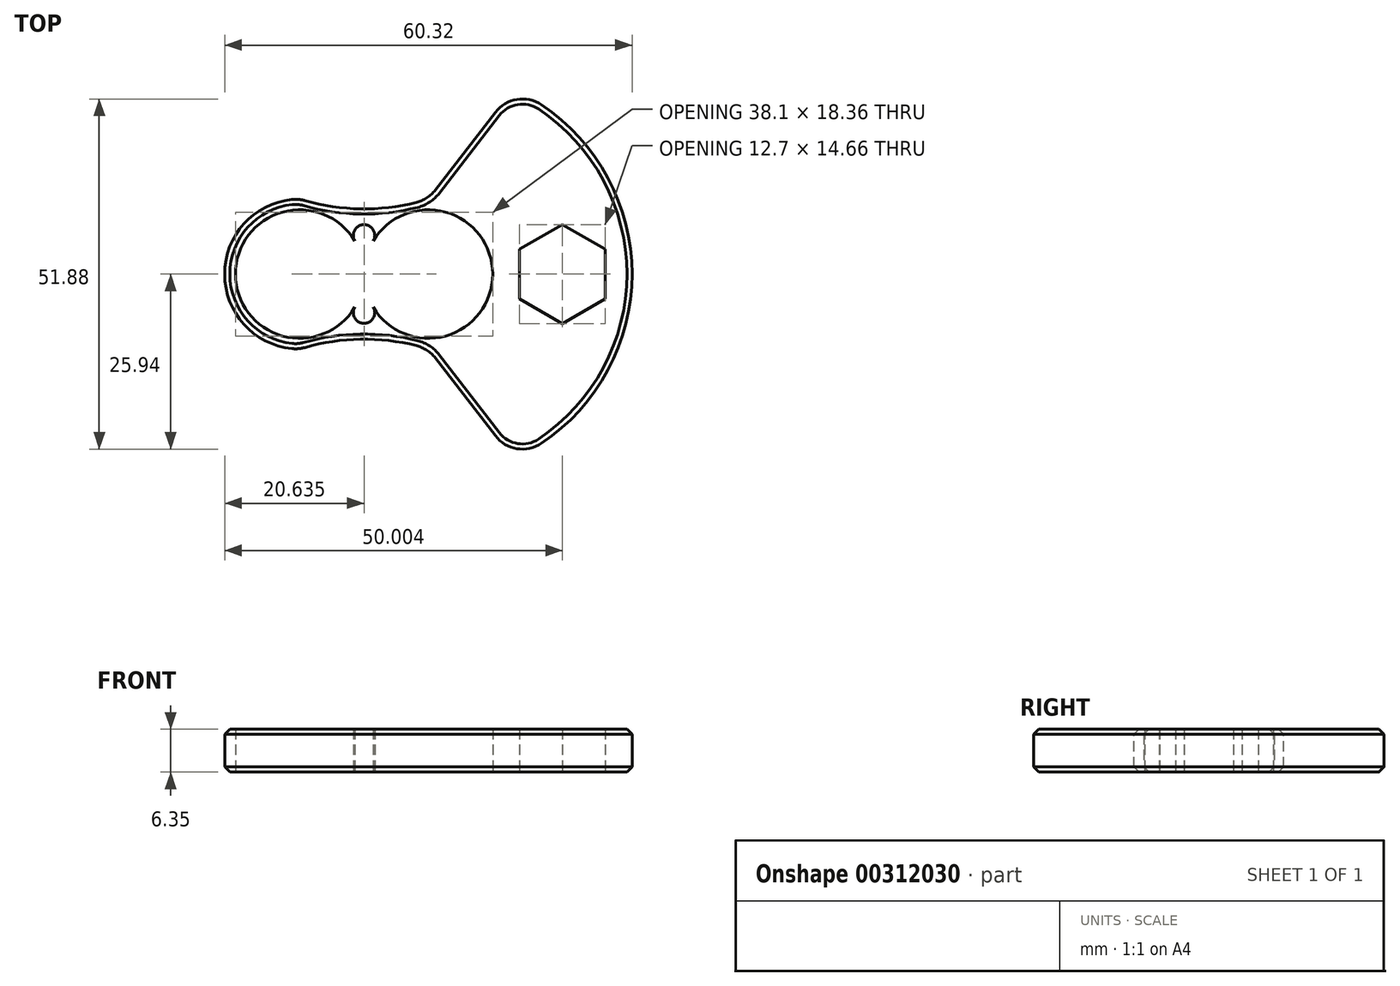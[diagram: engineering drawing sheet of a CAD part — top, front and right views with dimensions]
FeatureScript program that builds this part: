
annotation { "Feature Type Name" : "Feature", "Feature Type Description" : "" }
export const myFeature = defineFeature(function(context is Context, id is Id, definition is map)
    precondition{}
    {
        {
            var Q0;
            Q0=qCreatedBy(makeId("Top.planeOp"),FACE);
            var sketch = newSketch(context, id + "F0", { "sketchPlane" : qUnion([Q0])});
            skArc(sketch, "E0", {"start": v(-8.16, -4.9) * mm, "mid": v(9.52, 0) * mm, "end": v(-8.16, 4.9) * mm});
            skArc(sketch, "E1", {"start": v(-10.89, 4.9) * mm, "mid": v(-28.58, 0) * mm, "end": v(-10.89, -4.9) * mm});
            skArc(sketch, "E2", {"start": v(-19.05, 11.11) * mm, "mid": v(-30.16, 0) * mm, "end": v(-19.05, -11.11) * mm});
            skLineSegment(sketch, "E3", {"start": v(0, -11.11) * mm, "end": v(12.58, -27.42) * mm});
            skLineSegment(sketch, "E4", {"start": v(0, 11.11) * mm, "end": v(12.58, 27.42) * mm});
            skArc(sketch, "E5", {"start": v(-10.89, -4.9) * mm, "mid": v(-9.52, -7.31) * mm, "end": v(-8.16, -4.9) * mm});
            skArc(sketch, "E6", {"start": v(-8.16, 4.9) * mm, "mid": v(-9.53, 7.31) * mm, "end": v(-10.89, 4.9) * mm});
            skArc(sketch, "E7", {"start": v(12.58, -27.42) * mm, "mid": v(30.16, 0) * mm, "end": v(12.58, 27.42) * mm});
            skArc(sketch, "E8", {"start": v(-19.05, 11.11) * mm, "mid": v(-9.53, 9.65) * mm, "end": v(0, 11.11) * mm});
            skArc(sketch, "E9", {"start": v(0, -11.11) * mm, "mid": v(-9.53, -9.65) * mm, "end": v(-19.05, -11.11) * mm});
            skLineSegment(sketch, "E10.0", {"start": v(13.5, -3.67) * mm, "end": v(13.5, 3.67) * mm});
            skLineSegment(sketch, "E10.1", {"start": v(13.5, 3.67) * mm, "end": v(19.84, 7.33) * mm});
            skLineSegment(sketch, "E10.2", {"start": v(19.84, 7.33) * mm, "end": v(26.2, 3.67) * mm});
            skLineSegment(sketch, "E10.3", {"start": v(26.2, 3.67) * mm, "end": v(26.2, -3.67) * mm});
            skLineSegment(sketch, "E10.4", {"start": v(26.2, -3.67) * mm, "end": v(19.84, -7.33) * mm});
            skLineSegment(sketch, "E10.5", {"start": v(19.84, -7.33) * mm, "end": v(13.5, -3.67) * mm});
            skPoint(sketch, "E10.0.midPoint", {"position": v(13.5, 0) * mm});
            skPoint(sketch, "E11.center.orphan", {"position": v(19.84, 0) * mm});
            skPoint(sketch, "E12.start.orphan", {"position": v(9.52, 0) * mm});
            skPoint(sketch, "E13.trimOffspring.end.orphan", {"position": v(30.16, 0) * mm});
            skSolve(sketch);
        }
        {
            var Q0;
            Q0=makeQuery(id+"F0.imprint","IMPRINT",FACE,{"disambiguationData":[TD([[makeQuery(id+"F0.imprint","IMPRINT",EDGE,{"derivedFrom":sQuery(id+"F0.wireOp",EDGE,"E0")}),-1.0]])]});
            extrude(context, id + "F1", {"entities" : qUnion([Q0]), "depth" : 6.35 * mm, "offsetDistance" : 25.4 * mm});
        }
        {
            var Q0;
            Q0=makeQuery(id+"F1.opExtrude","SWEPT_EDGE",EDGE,{"disambiguationData":[OSD([sQuery(id+"F0.wireOp",EDGE,"kZLvEBYJ-JnEX-xgXO-vPxD-7ih4jmy4RvpC"),sQuery(id+"F0.wireOp",EDGE,"E3")])]});
            var Q1;
            Q1=makeQuery(id+"F1.opExtrude","SWEPT_EDGE",EDGE,{"disambiguationData":[OSD([sQuery(id+"F0.wireOp",EDGE,"kZLvEBYJ-JnEX-xgXO-vPxD-7ih4jmy4RvpC"),sQuery(id+"F0.wireOp",EDGE,"E4")])]});
            var Q2;
            Q2=makeQuery(id+"F1.opExtrude","SWEPT_EDGE",EDGE,{"disambiguationData":[OSD([sQuery(id+"F0.wireOp",EDGE,"E2"),sQuery(id+"F0.wireOp",EDGE,"AoVct10g-OvvF-BB1q-fatW-92vV8a4QILmj")])]});
            var Q3;
            Q3=makeQuery(id+"F1.opExtrude","SWEPT_EDGE",EDGE,{"disambiguationData":[OSD([sQuery(id+"F0.wireOp",EDGE,"E2"),sQuery(id+"F0.wireOp",EDGE,"D37h3eVz-aBzz-mAJ8-7cKl-PauLEiSiHLsy")])]});
            var Q4;
            Q4=makeQuery(id+"F1.opExtrude","SWEPT_EDGE",EDGE,{"disambiguationData":[OSD([sQuery(id+"F0.wireOp",EDGE,"E3"),sQuery(id+"F0.wireOp",EDGE,"AoVct10g-OvvF-BB1q-fatW-92vV8a4QILmj")])]});
            var Q5;
            Q5=makeQuery(id+"F1.opExtrude","SWEPT_EDGE",EDGE,{"disambiguationData":[OSD([sQuery(id+"F0.wireOp",EDGE,"E4"),sQuery(id+"F0.wireOp",EDGE,"D37h3eVz-aBzz-mAJ8-7cKl-PauLEiSiHLsy")])]});
            fillet(context, id + "F2", {"entities" : qUnion([Q0, Q1, Q2, Q3, Q4, Q5]), "radius" : 5.08 * mm, "tangentPropagation" : true, "allowEdgeOverflow" : false});
        }
        {
            var Q0;
            Q0=makeQuery(id+"F1.opExtrude","CAP_EDGE",EDGE,{"disambiguationData":[OSD([sQuery(id+"F0.wireOp",EDGE,"E7")])],"isStart":false});
            var Q1;
            Q1=makeQuery(id+"F1.opExtrude","CAP_EDGE",EDGE,{"disambiguationData":[OSD([sQuery(id+"F0.wireOp",EDGE,"E7")])],"isStart":true});
            chamfer(context, id + "F3", {"entities" : qUnion([Q0, Q1]), "width" : 0.76 * mm, "tangentPropagation" : true});
        }
    });
